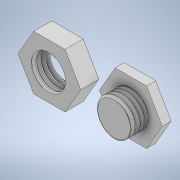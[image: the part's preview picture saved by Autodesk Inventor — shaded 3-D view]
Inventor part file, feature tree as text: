
AUTODESK INVENTOR PART (.ipt)
format: ipt  version: 2021.1 (Build 251245000, 245)  size: 408,064 bytes
history: native  units: in
note: dims shown in document units (in); Inventor stores cm internally (conversion verified against a paired STEP export)
features: sketch x7, extrude x4, helix x2
ambient origin geometry x8: Origin, YZ Plane, XZ Plane, XY Plane, X Axis, Y Axis, Z Axis, Center Point
bodies: Solid1 (feature_tree)
feature tree (13):
  extrude  "Extrusion1"  Depth=0.25in TaperAngle=0.0deg
  extrude  "Extrusion3"  TaperAngle=60.0deg  [1 undecoded]
  helix  "Coil1"  [1 undecoded]
  sketch  "Sketch5"  dims[d12=0.9755in d13=0.125in d14=0.125in]
  extrude  "Extrusion4"  Depth=0.0119in
  extrude  "Extrusion5"  Depth=0.125in
  helix  "Coil2"  [1 undecoded]
  sketch  "Sketch1"  dims[d0=1.5in d1=0.25in d2=0.0in]
  sketch  "Sketch3"  dims[d6=0.5in d7=0.0in d8=60.0deg d9=0.4878in]
  sketch  "Sketch4"  dims[d10=0.0119in d11=0.4066in]
  sketch  "Sketch6"  dims[d15=0.75in]
  sketch  "Sketch7"  dims[d16=0.3937in d17=0.0in d18=90.0deg d19=90.0deg d20=0.0in d21=0.0in]
  sketch  "Sketch9"  dims[d22=2.0in d23=1.5in d24=0.5in d25=0.0in d26=0.8897in d27=0.0in d28=0.0in d29=60.0deg d30=0.4449in d31=0.0119in d32=0.5156in d33=0.125in d34=0.75in d35=0.3937in d36=0.0in d37=90.0deg d38=90.0deg d39=0.0in d40=0.0in d41=0.125in]
note: 3 required parameter values undecoded (feature->parameter linkage not recoverable at this tier; creation-order binding heuristic only, values carry confidence <= 0.55)
